# Revit family: Wye-Pattern_Strainers-Backflow_Preventor-WATTS-77F-DI-250
name_source: partatom
category: Pipe Accessories
revit_build: Autodesk Revit 2014 (Build: 20130308_1515(x64)
units: mm (PartAtom-declared; Revit-internal decimal feet)

## types (9) — shared parameters
Assembly Code = F1050
CW Connection = Yes
Clearance = Yes
Description = Ductile Iron, Class 250 Flanged End, Wye-Pattern Strainers
Finish = Metal-Watts-Ductile Iron
HW Connection = No
Manufacturer = WATTS
Material = Metal-Watts-Ductile Iron
Max. Working Pressure = 500psi (34.47 bars) WOG, non-shock, @ 150°F (66°C) 250psi (17.2 bars) WSP @ 406°F (208°C)
Model = 77F-DI-250
Price = Prices may vary. Please consult Manufacturer Representative for most up-to-date price list.
Product Documentation Link = http://media.wattswater.com
Product Page URL = http://www.watts.com
URL = http://www.watts.com
Vent Connection = No
Waste Connection = No

## per-type parameters (varying)
| type | A | B | Body Radius | Connection Inlet Description | Connection Outlet Description | Connection Radius | Connection Size | D | Flange Thickness | NPT Diameter | NPT Radius | Nominal Depth | Nominal Depth 2 | Strainer Diameter | Strainer Length | Strainer Offset Length From Flange | Strainer Revolve Offset Distance | Strainer Thickness | Strainer Width | Weight | Width |
| 77F-DI-250 2" | 8 7/8" | 6 1/2" | 1 1/4" | 1/2" Flanged Inlet | 1/2" Flanged Outlet | 1" | 2" | 9 1/8" | 3/8" | 1/2" | 1/4" | 1" | 1/2" | 2 1/2" | 3 7/8" | 11/16" | 1 15/16" | 3/4" | 3 7/8" | 28/13 (LB/KG) | 4 1/4" |
| 77F-DI-250 2.5" | 11 1/4" | 7" | 1 5/8" | 1" Flanged Inlet | 1" Flanged Outlet | 1 1/4" | 2 1/2" | 9 7/8" | 3/8" | 1" | 1/2" | 1" | 1/2" | 3" | 4 7/8" | 15/16" | 2 7/16" | 3/4" | 4 7/8" | 38/17 (LB/KG) | 5" |
| 77F-DI-250 3" | 11 5/8" | 8" | 2" | 1" Flanged Inlet | 1" Flanged Outlet | 1 1/2" | 3" | 11 1/4" | 1/2" | 1" | 1/2" | 1 3/8" | 11/16" | 3 3/4" | 5" | 5/8" | 2 1/2" | 1" | 5" | 54/24 (LB/KG) | 5 1/2" |
| 77F-DI-250 4" | 14 1/2" | 10 3/4" | 2 1/2" | 1" Flanged Inlet | 1" Flanged Outlet | 2" | 4" | 15" | 1/2" | 1" | 1/2" | 1 5/8" | 13/16" | 4 1/4" | 6 1/8" | 15/16" | 3 1/16" | 1" | 6 1/8" | 110/50 (LB/KG) | 7" |
| 77F-DI-250 5" | 17 3/8" | 13 1/2" | 3" | 1-1/4" Flanged Inlet | 1-1/4" Flanged Outlet | 2 1/2" | 5" | 19" | 5/8" | 1 1/4" | 5/8" | 1 3/4" | 7/8" | 4 3/4" | 7 1/2" | 1 3/8" | 3 3/4" | 1 1/4" | 7 1/2" | 160/73 (LB/KG) | 8 1/4" |
| 77F-DI-250 6" | 18 3/4" | 16 1/4" | 3 1/2" | 1-1/2" Flanged Inlet | 1-1/2" Flanged Outlet | 3" | 6" | 22 3/4" | 1" | 1 1/2" | 3/4" | 2 1/2" | 1 1/4" | 6 1/2" | 8 1/2" | 1" | 4 1/4" | 2" | 8 1/2" | 224/102 (LB/KG) | 10" |
| 77F-DI-250 8" | 21 7/8" | 19 1/2" | 5" | 1-1/2" Flanged Inlet | 1-1/2" Flanged Outlet | 4" | 8" | 27 3/4" | 1" | 1 1/2" | 3/4" | 3 7/8" | 1 15/16" | 9 1/4" | 11" | 7/8" | 5 1/2" | 2" | 11" | 468/212 (LB/KG) | 14" |
| 77F-DI-250 10" | 27 1/4" | 21 1/4" | 5 5/8" | 2" Flanged Inlet | 2" Flanged Outlet | 5" | 10" | 29 3/4" | 1 1/2" | 2" | 1" | 4" | 2" | 10" | 12" | 1" | 6" | 3" | 12" | 590/268 (LB/KG) | 16" |
| 77F-DI-250 12" | 31 3/8" | 25" | 7" | 2" Flanged Inlet | 2" Flanged Outlet | 6" | 12" | 35" | 1 1/2" | 2" | 1" | 5 3/4" | 2 7/8" | 13 1/2" | 15" | 3/4" | 7 1/2" | 3" | 15" | 890/404 (LB/KG) | 20" |

## geometry (parser evidence)
native form markers: Revolve x1, Sweep x1
no freeform markers — native parametric forms only
